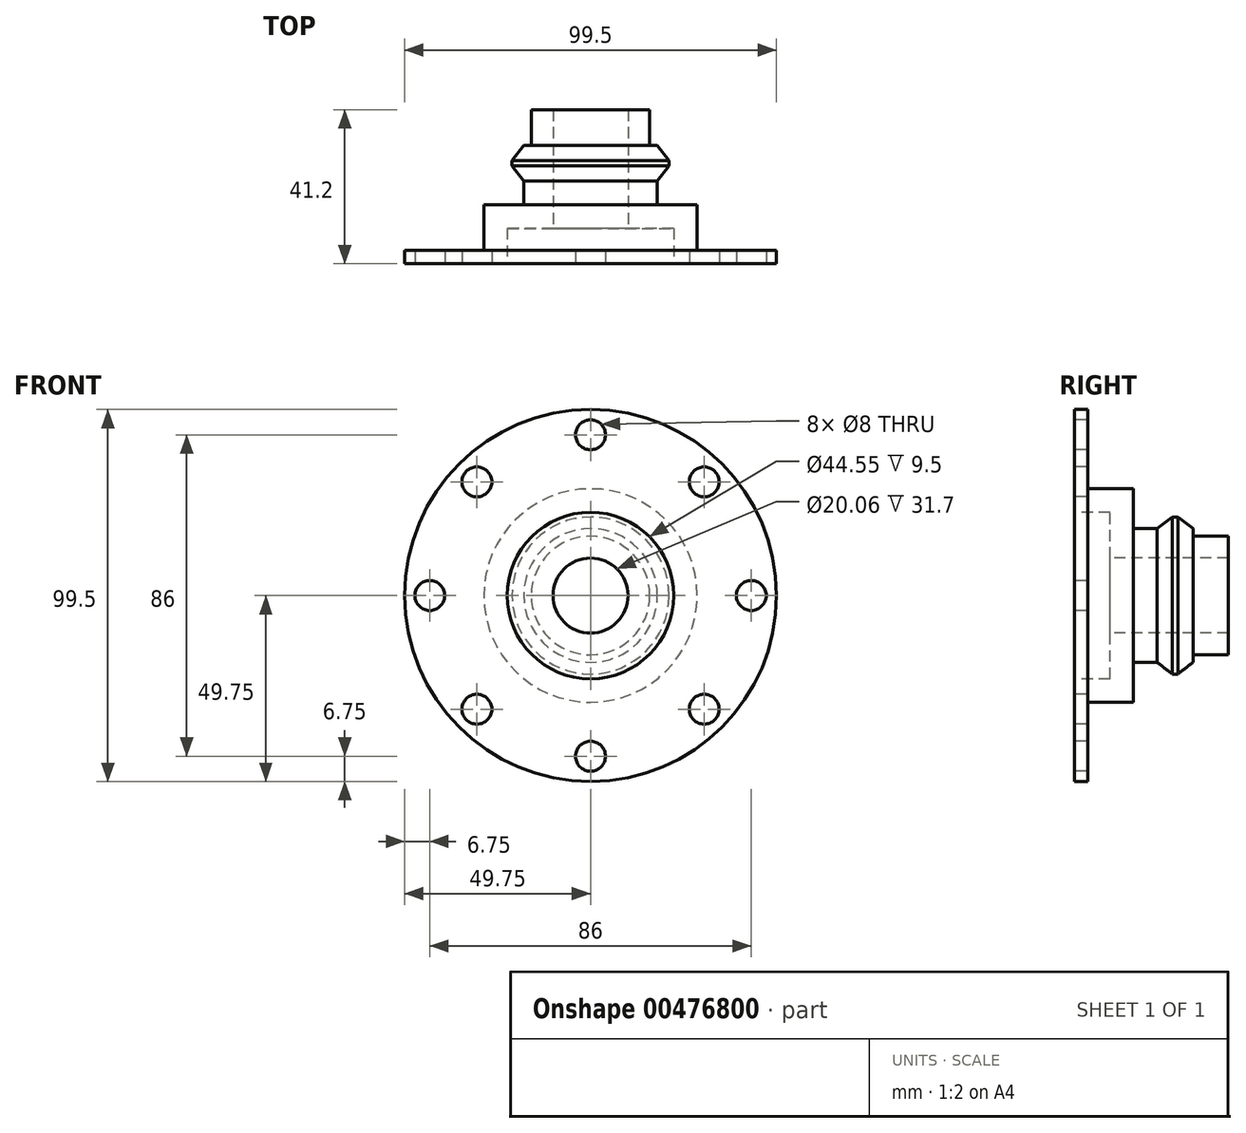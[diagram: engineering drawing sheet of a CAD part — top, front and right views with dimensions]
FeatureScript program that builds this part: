
annotation { "Feature Type Name" : "Feature", "Feature Type Description" : "" }
export const myFeature = defineFeature(function(context is Context, id is Id, definition is map)
    precondition{}
    {
        {
            var Q0;
            Q0=qCreatedBy(makeId("Right.planeOp"),FACE);
            var sketch = newSketch(context, id + "F0", { "sketchPlane" : qUnion([Q0])});
            skLineSegment(sketch, "E0", {"start": v(0, 22.28) * mm, "end": v(0, 49.75) * mm});
            skLineSegment(sketch, "E1", {"start": v(0, 49.75) * mm, "end": v(3.55, 49.75) * mm});
            skLineSegment(sketch, "E2", {"start": v(3.55, 49.75) * mm, "end": v(3.55, 28.55) * mm});
            skLineSegment(sketch, "E3", {"start": v(3.55, 28.55) * mm, "end": v(15.75, 28.55) * mm});
            skLineSegment(sketch, "E4", {"start": v(15.75, 28.55) * mm, "end": v(15.75, 17.87) * mm});
            skLineSegment(sketch, "E5", {"start": v(15.75, 17.88) * mm, "end": v(22.1, 17.88) * mm});
            skLineSegment(sketch, "E6", {"start": v(22.1, 17.88) * mm, "end": v(26.15, 21) * mm});
            skLineSegment(sketch, "E7", {"start": v(26.15, 21) * mm, "end": v(27.65, 21) * mm});
            skLineSegment(sketch, "E8", {"start": v(31.7, 15.85) * mm, "end": v(41.2, 15.85) * mm});
            skLineSegment(sketch, "E9", {"start": v(9.5, 22.27) * mm, "end": v(0, 22.27) * mm});
            skLineSegment(sketch, "E10", {"start": v(9.5, 22.27) * mm, "end": v(9.5, 10.03) * mm});
            skLineSegment(sketch, "E11", {"start": v(9.5, 10.03) * mm, "end": v(41.2, 10.03) * mm});
            skLineSegment(sketch, "E12", {"start": v(41.2, 10.03) * mm, "end": v(41.2, 15.85) * mm});
            skLineSegment(sketch, "E13", {"start": v(0, 0) * mm, "end": v(5001.89, 0) * mm, "construction": true});
            skLineSegment(sketch, "E14", {"start": v(31.7, 15.85) * mm, "end": v(31.7, 17.87) * mm});
            skLineSegment(sketch, "E15", {"start": v(31.7, 17.87) * mm, "end": v(27.65, 21) * mm});
            skLineSegment(sketch, "E16", {"start": v(22.1, 17.88) * mm, "end": v(31.7, 17.88) * mm, "construction": true});
            skSolve(sketch);
        }
        {
            var Q0;
            Q0=makeQuery(id+"F0.imprint","IMPRINT",FACE,{"disambiguationData":[TD([[makeQuery(id+"F0.imprint","IMPRINT",EDGE,{"derivedFrom":sQuery(id+"F0.wireOp",EDGE,"E0")}),-1.0]])]});
            var Q1;
            Q1=sQuery(id+"F0.wireOp",EDGE,"E13");
            revolve(context, id + "F1", {"entities" : qUnion([Q0]), "axis" : qUnion([Q1]), "revolveType" : RevolveType.FULL});
        }
        {
            var Q0;
            Q0=makeQuery(id+"F1.opRevolve","SWEPT_FACE",FACE,{"disambiguationData":[OSD([sQuery(id+"F0.wireOp",EDGE,"E2")])]});
            var sketch = newSketch(context, id + "F2", { "sketchPlane" : qUnion([Q0])});
            skCircle(sketch, "E17", {"center": v(0, 0) * mm, "radius": 43 * mm, "construction": true});
            skCircle(sketch, "E18", {"center": v(0, 43) * mm, "radius": 4 * mm});
            skLineSegment(sketch, "E19", {"start": v(0, 0) * mm, "end": v(-43, 0) * mm, "construction": true});
            skLineSegment(sketch, "E20", {"start": v(-43, 0) * mm, "end": v(0, 43) * mm, "construction": true});
            skLineSegment(sketch, "E21", {"start": v(0, 0) * mm, "end": v(43, 0) * mm, "construction": true});
            skLineSegment(sketch, "E22", {"start": v(43, 0) * mm, "end": v(0, -43) * mm, "construction": true});
            skLineSegment(sketch, "E23", {"start": v(0, -43) * mm, "end": v(-43, 0) * mm, "construction": true});
            skLineSegment(sketch, "E24", {"start": v(-21.5, -21.5) * mm, "end": v(-30.4, -30.4) * mm, "construction": true});
            skLineSegment(sketch, "E25", {"start": v(21.5, -21.5) * mm, "end": v(30.4, -30.4) * mm, "construction": true});
            skLineSegment(sketch, "E26", {"start": v(43, 0) * mm, "end": v(0, 43) * mm, "construction": true});
            skLineSegment(sketch, "E27", {"start": v(21.5, 21.5) * mm, "end": v(30.4, 30.4) * mm, "construction": true});
            skCircle(sketch, "E28", {"center": v(-30.4, 30.4) * mm, "radius": 4 * mm});
            skCircle(sketch, "E29", {"center": v(43, 0) * mm, "radius": 4 * mm});
            skCircle(sketch, "E30", {"center": v(30.4, 30.4) * mm, "radius": 4 * mm});
            skCircle(sketch, "E31", {"center": v(-30.4, -30.4) * mm, "radius": 4 * mm});
            skCircle(sketch, "E32", {"center": v(-43, 0) * mm, "radius": 4 * mm});
            skCircle(sketch, "E33", {"center": v(0, -43) * mm, "radius": 4 * mm});
            skCircle(sketch, "E34", {"center": v(30.4, -30.4) * mm, "radius": 4 * mm});
            skLineSegment(sketch, "E35", {"start": v(-21.5, 21.5) * mm, "end": v(-30.4, 30.4) * mm, "construction": true});
            skSolve(sketch);
        }
        {
            var Q0;
            Q0 = qSketchRegion(id + "F2", true);
            extrude(context, id + "F3", {"entities" : qUnion([Q0]), "operationType" : NewBodyOperationType.REMOVE, "endBound" : BoundingType.SYMMETRIC, "depth" : 508 * mm});
        }
    });
